# Revit family: Reece_Bath_Roca_The Gap_Inset Bath_1700mm
name_source: partatom
category: Plumbing Fixtures
revit_build: Autodesk Revit 2018 (Build: 20180329_1100(x64)
units: mm (PartAtom-declared; Revit-internal decimal feet)

## family parameters
Cut with Voids When Loaded = Yes
Host = Face
Part Type = Normal
Room Calculation Point = Yes
Round Connector Dimension = Use Diameter
Shared = Yes

## types (1)
- White
    Default Elevation = 0 mm  [stored 0 ft]
    Description = Roca The Gap Inset Bath (with Overflow) 1700 x 750mm White
    Disclaimer = THIS FILE IS THE PROPERTY OF THE REECE GROUP. IT MAY NOT BE REPRODUCED, REVERSE-ENGINEERED OR MODIFIED. ANY REPUBLICATION, TRANSMISSION OR DISTRIBUTION FOR THE PURPOSE OF COMMERCIALLY EXPLOITING THE FILES IS PROHIBITED.
    Keynote = Product #9505307, Reece_Bath_Roca_The Gap_Inset Bath_1700mm - White
    Manufacturer = Roca
    Model = The Gap
    Reece_Bath_Lip = 30 mm
    Reece_Bath_Outlet = 52 mm
    Reece_Detail_Additional = Overflow
    Reece_Detail_Disclaimer = THIS FILE IS THE PROPERTY OF THE REECE GROUP. IT MAY NOT BE REPRODUCED, REVERSE-ENGINEERED OR MODIFIED. ANY REPUBLICATION, TRANSMISSION OR DISTRIBUTION FOR THE PURPOSE OF COMMERCIALLY EXPLOITING THE FILES IS PROHIBITED.
    Reece_Detail_Installation = Inset Bath
    Reece_Material_Main = Reece_Acrylic_White
    Reece_Material_Secondary = Reece_Brass_Chrome
    Reece_Overall_Capacity = 215 L
    Reece_Overall_Depth = 420 mm
    Reece_Overall_Height = 432 mm
    Reece_Overall_Length = 1700 mm  [stored 5.57743 ft]
    Reece_Overall_Width = 750 mm  [stored 2.46063 ft]
    Reece_Product_Brand = Roca
    Reece_Product_Description = Roca The Gap Inset Bath with Overflow 1700 x 750mm White
    Reece_Product_Mount = Inset
    Reece_Product_Number = 9505307
    Reece_Product_Sub Brand = The Gap
    Reece_Product_Type = Bath
    Reece_Product_Web Page = https://www.reece.com.au
    Type Comments = Bath
    URL = https://www.reece.com.au

note: [stored X ft] marks values corroborated as IEEE doubles in the binary element streams (Revit-internal decimal feet)

## geometry (parser evidence)
native form markers: Sweep x5
no freeform markers — native parametric forms only
